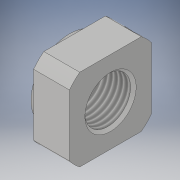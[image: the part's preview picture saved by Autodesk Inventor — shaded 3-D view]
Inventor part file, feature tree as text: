
AUTODESK INVENTOR PART (.ipt)
format: ipt  version: 2021 (Build 250183000, 183)  size: 164,352 bytes
history: native  units: mm
features: other x7, sketch x4, revolve x3, thread x2, extrude x1
ambient origin geometry x8: Origin, YZ Plane, XZ Plane, XY Plane, X Axis, Y Axis, Z Axis, Center Point
bodies: Solid1 (feature_tree)
feature tree (17):
  extrude  "Extrusion1"  TaperAngle=360.0deg  [1 undecoded]
  revolve  "Revolution1"  [1 undecoded]
  revolve  "Revolution2"  [1 undecoded]
  thread  "Thread1"  [1 undecoded]
  revolve  "Revolution3"  [1 undecoded]
  thread  "Thread2"  [1 undecoded]
  other  "to_collar_XY"
  other  "to_collar_YZ"
  other  "to_collar_ZX"
  other  "to_collar_X"
  other  "to_collar_Y"
  other  "to_collar_Z"
  other  "to_collar_Center"
  sketch  "Sketch_1"  dims[d0=7.0mm d1=0.0mm d2=360.0deg]
  sketch  "Sketch_2"  dims[d3=360.0deg d4=6.917mm d5=0.0mm]
  sketch  "Sketch_3"  dims[d6=360.0deg d7=5.7295mm d8=0.0mm d9=0.0mm]
  sketch  "Sketch_4"
note: 6 required parameter values undecoded (feature->parameter linkage not recoverable at this tier; creation-order binding heuristic only, values carry confidence <= 0.55)